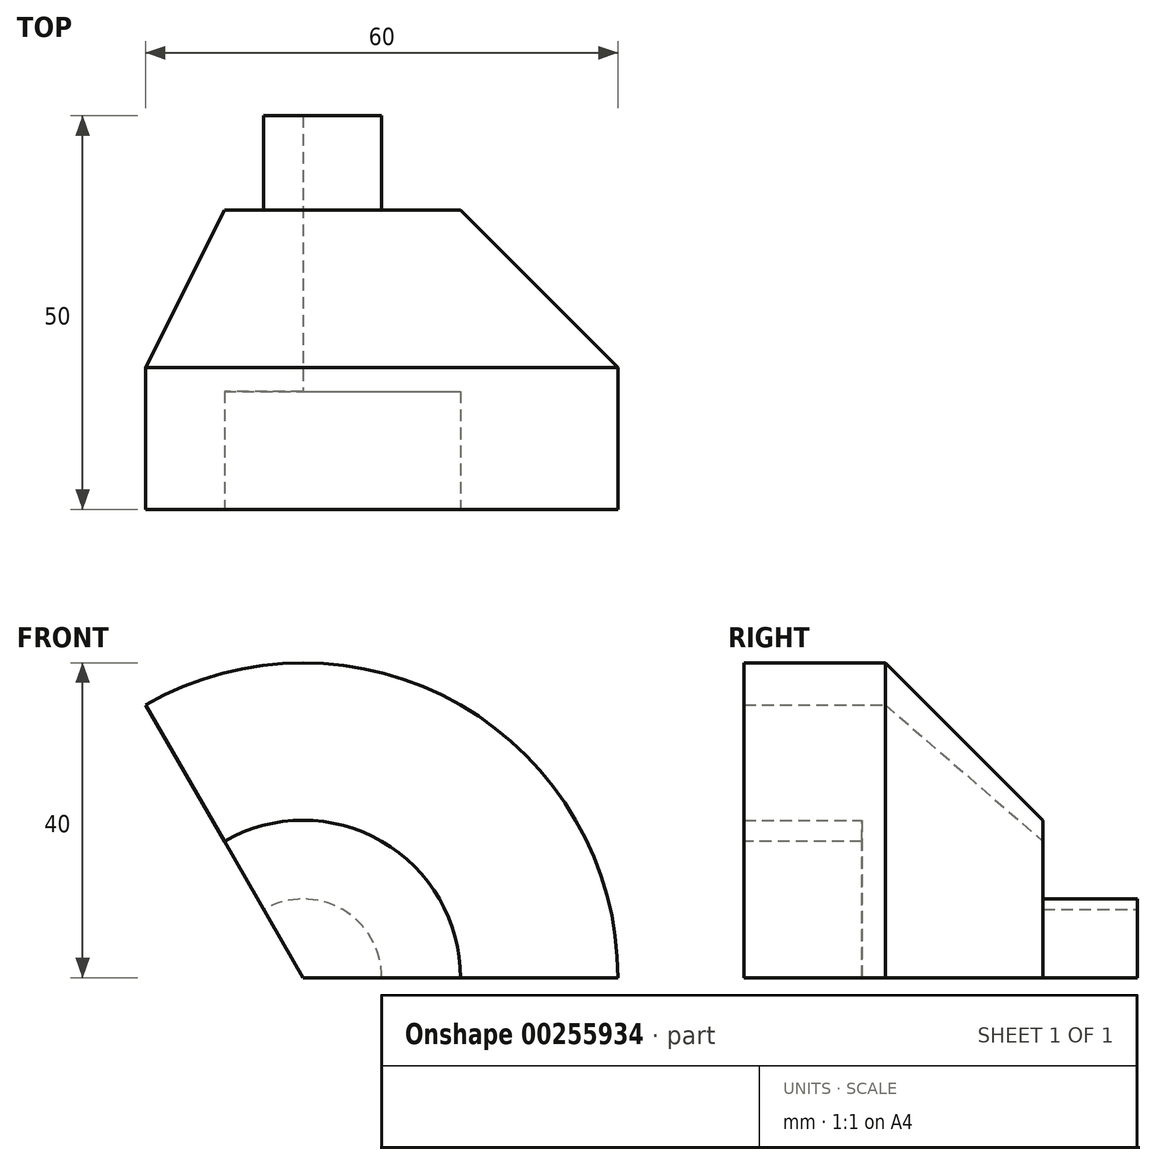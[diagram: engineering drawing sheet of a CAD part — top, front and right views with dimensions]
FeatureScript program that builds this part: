
annotation { "Feature Type Name" : "Feature", "Feature Type Description" : "" }
export const myFeature = defineFeature(function(context is Context, id is Id, definition is map)
    precondition{}
    {
        {
            var Q0;
            Q0=qCreatedBy(makeId("Top.planeOp"),FACE);
            var sketch = newSketch(context, id + "F0", { "sketchPlane" : qUnion([Q0])});
            skLineSegment(sketch, "E0", {"start": v(0, 35) * mm, "end": v(0, 0) * mm});
            skLineSegment(sketch, "E1", {"start": v(0, 0) * mm, "end": v(20, 0) * mm});
            skLineSegment(sketch, "E2", {"start": v(20, 0) * mm, "end": v(20, -15) * mm});
            skLineSegment(sketch, "E3", {"start": v(20, -15) * mm, "end": v(40, -15) * mm});
            skLineSegment(sketch, "E4", {"start": v(40, -15) * mm, "end": v(40, 3) * mm});
            skLineSegment(sketch, "E5", {"start": v(40, 3) * mm, "end": v(20, 23) * mm});
            skLineSegment(sketch, "E6", {"start": v(20, 23) * mm, "end": v(10, 23) * mm});
            skLineSegment(sketch, "E7", {"start": v(10, 23) * mm, "end": v(10, 35) * mm});
            skLineSegment(sketch, "E8", {"start": v(10, 35) * mm, "end": v(0, 35) * mm});
            skSolve(sketch);
        }
        {
            var Q0;
            Q0=makeQuery(id+"F0.imprint","IMPRINT",FACE,{"disambiguationData":[TD([[makeQuery(id+"F0.imprint","IMPRINT",EDGE,{"derivedFrom":sQuery(id+"F0.wireOp",EDGE,"E0")}),1.0]])]});
            var Q1;
            Q1=sQuery(id+"F0.wireOp",EDGE,"E0");
            revolve(context, id + "F1", {"entities" : qUnion([Q0]), "axis" : qUnion([Q1]), "revolveType" : RevolveType.ONE_DIRECTION, "angle" : 120 * degree});
        }
    });
